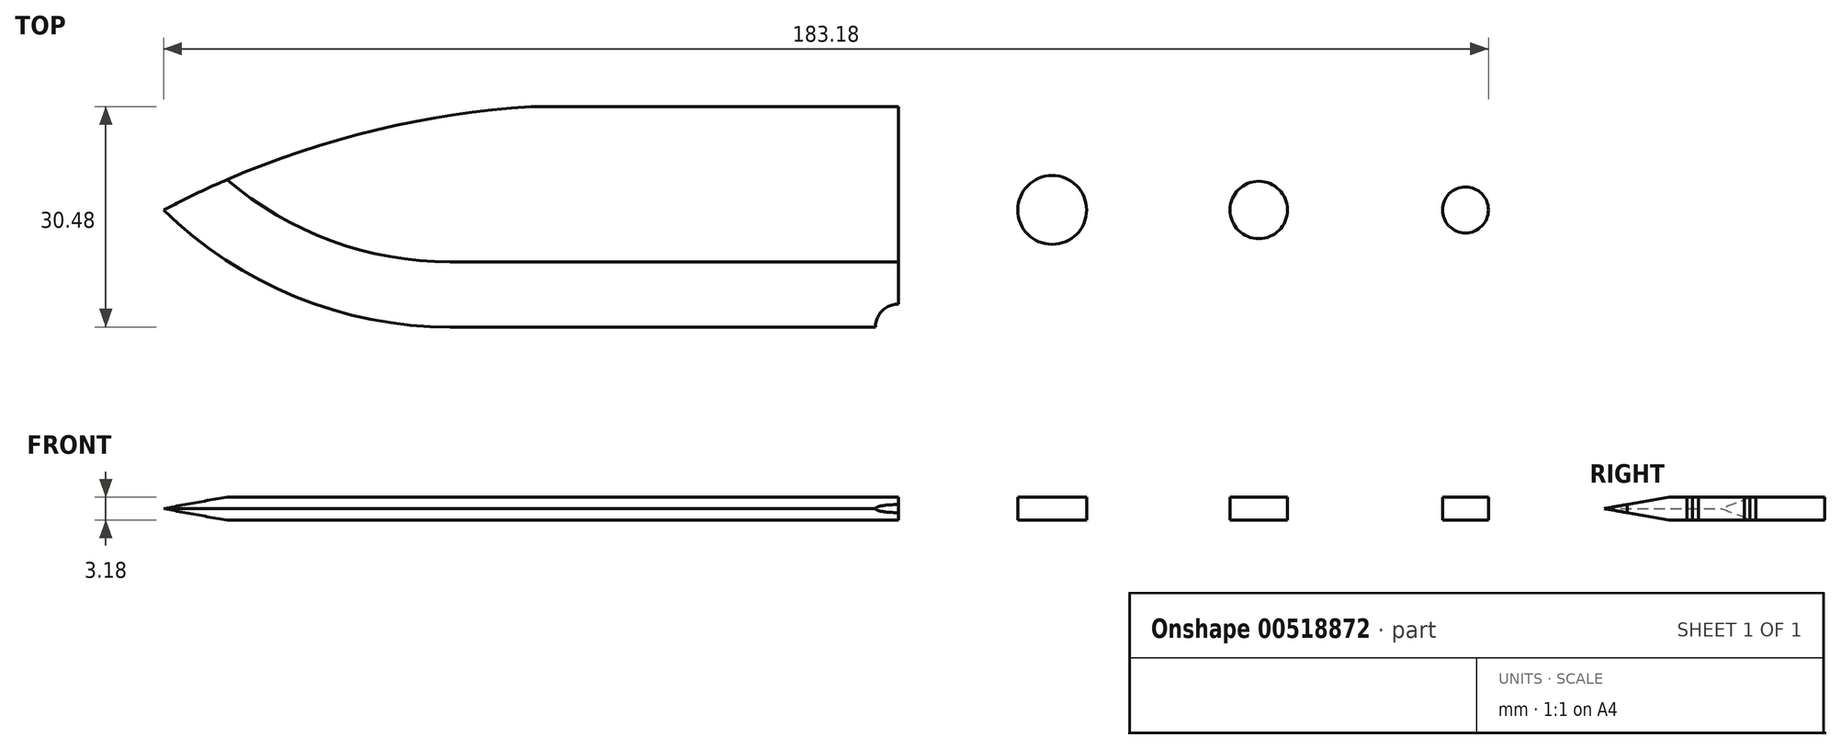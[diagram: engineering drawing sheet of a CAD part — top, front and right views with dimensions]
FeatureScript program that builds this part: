
annotation { "Feature Type Name" : "Feature", "Feature Type Description" : "" }
export const myFeature = defineFeature(function(context is Context, id is Id, definition is map)
    precondition{}
    {
        {
            var Q0;
            Q0=qCreatedBy(makeId("Top.planeOp"),FACE);
            var sketch = newSketch(context, id + "F0", { "sketchPlane" : qUnion([Q0])});
            skLineSegment(sketch, "E0", {"start": v(0, 0) * mm, "end": v(203.2, 0) * mm});
            skLineSegment(sketch, "E1", {"start": v(203.2, 0) * mm, "end": v(203.2, -38.1) * mm});
            skLineSegment(sketch, "E2", {"start": v(203.2, -38.1) * mm, "end": v(0, -38.1) * mm});
            skLineSegment(sketch, "E3", {"start": v(0, -38.1) * mm, "end": v(0, 0) * mm});
            skSolve(sketch);
        }
        {
            var Q0;
            Q0=qSketchRegion(id+"F0",true);
            extrude(context, id + "F1", {"entities" : qUnion([Q0]), "depth" : 3.17 * mm});
        }
        {
            var Q0;
            Q0=makeQuery(id+"F1.opExtrude","CAP_FACE",FACE,{"disambiguationData":[OSD([sQuery(id+"F0.wireOp",EDGE,"E0"),sQuery(id+"F0.wireOp",EDGE,"E1"),sQuery(id+"F0.wireOp",EDGE,"E2"),sQuery(id+"F0.wireOp",EDGE,"E3")])],"isStart":false});
            var sketch = newSketch(context, id + "F2", { "sketchPlane" : qUnion([Q0])});
            skLineSegment(sketch, "E4", {"start": v(101.6, 0) * mm, "end": v(101.6, -38.1) * mm});
            skLineSegment(sketch, "E5", {"start": v(0, 0) * mm, "end": v(0, -19.05) * mm});
            skLineSegment(sketch, "E6", {"start": v(0, -9.53) * mm, "end": v(0, -19.05) * mm});
            skLineSegment(sketch, "E7", {"start": v(0, 0) * mm, "end": v(101.6, 0) * mm});
            skLineSegment(sketch, "E8", {"start": v(39.6, -30.48) * mm, "end": v(101.6, -30.48) * mm});
            skArc(sketch, "E9", {"start": v(50.8, 0) * mm, "mid": v(24.65, -4.48) * mm, "end": v(0, -14.29) * mm});
            skCircle(sketch, "E10", {"center": v(101.6, -30.48) * mm, "radius": 3.18 * mm});
            skLineSegment(sketch, "E11", {"start": v(101.6, -30.48) * mm, "end": v(126.72, -30.48) * mm});
            skLineSegment(sketch, "E12", {"start": v(101.6, -33.65) * mm, "end": v(126.77, -33.65) * mm});
            skLineSegment(sketch, "E13", {"start": v(104.78, -30.48) * mm, "end": v(104.78, -33.65) * mm});
            skLineSegment(sketch, "E14", {"start": v(104.78, -33.65) * mm, "end": v(104.78, -38.1) * mm});
            skArc(sketch, "E15", {"start": v(134.38, -28.16) * mm, "mid": v(118.68, -26.05) * mm, "end": v(104.78, -33.66) * mm});
            skLineSegment(sketch, "E16", {"start": v(203.2, 0) * mm, "end": v(203.2, -19.05) * mm});
            skArc(sketch, "E17", {"start": v(193.68, -26.2) * mm, "mid": v(163.91, -23.67) * mm, "end": v(134.38, -28.16) * mm});
            skPoint(sketch, "E18", {"position": v(39.6, -30.48) * mm});
            skArc(sketch, "E19", {"start": v(0, -14.29) * mm, "mid": v(18.2, -26.28) * mm, "end": v(39.6, -30.48) * mm});
            skLineSegment(sketch, "E20", {"start": v(0, -14.29) * mm, "end": v(203.2, -14.29) * mm});
            skLineSegment(sketch, "E21", {"start": v(184.15, 0) * mm, "end": v(203.2, -14.29) * mm});
            skLineSegment(sketch, "E22", {"start": v(203.2, -14.29) * mm, "end": v(184.15, -38.1) * mm});
            skCircle(sketch, "E23", {"center": v(122.86, -14.29) * mm, "radius": 4.76 * mm});
            skCircle(sketch, "E24", {"center": v(180, -14.29) * mm, "radius": 3.18 * mm});
            skCircle(sketch, "E25", {"center": v(151.43, -14.29) * mm, "radius": 3.97 * mm});
            skSolve(sketch);
        }
        {
            var Q0;
            {var subQ0=sQuery(id+"F2.wireOp",EDGE,"E5");Q0=makeQuery(id+"F2.imprint","IMPRINT",FACE,{"disambiguationData":[TD([[makeQuery(id+"F2.imprint","IMPRINT",EDGE,{"derivedFrom":subQ0}),-1.0]])]});}
            var Q1;
            {var subQ0=sQuery(id+"F2.wireOp",EDGE,"hBmztbTj-tqe3-CgKz-6O3F-K7U5qk9btVsn");var subQ1=sQuery(id+"F2.wireOp",EDGE,"E8");var subQ2=makeQuery(id+"F2.imprint","INTERSECT",VERTEX,{"derivedFrom":[subQ1,subQ0]});Q1=makeQuery(id+"F2.imprint","IMPRINT",FACE,{"disambiguationData":[TD([[makeQuery(id+"F2.imprint","IMPRINT",EDGE,{"disambiguationData":[TD([[subQ2,-1.0]])],"derivedFrom":subQ1}),-1.0]])]});}
            var Q2;
            {var subQ5=sQuery(id+"F2.wireOp",EDGE,"E14");Q2=makeQuery(id+"F2.imprint","IMPRINT",FACE,{"disambiguationData":[TD([[makeQuery(id+"F2.imprint","IMPRINT",EDGE,{"derivedFrom":subQ5}),-1.0]])]});}
            var Q3;
            {var subQ3=sQuery(id+"F2.wireOp",EDGE,"E13");Q3=makeQuery(id+"F2.imprint","IMPRINT",FACE,{"disambiguationData":[TD([[makeQuery(id+"F2.imprint","IMPRINT",EDGE,{"derivedFrom":subQ3}),-1.0]])]});}
            var Q4;
            {var subQ0=sQuery(id+"F2.wireOp",EDGE,"E11");var subQ1=sQuery(id+"F2.wireOp",EDGE,"E4");var subQ2=makeQuery(id+"F2.imprint","INTERSECT",VERTEX,{"derivedFrom":[subQ1,sQuery(id+"F2.wireOp",EDGE,"E8"),subQ0]});Q4=makeQuery(id+"F2.imprint","IMPRINT",FACE,{"disambiguationData":[TD([[makeQuery(id+"F2.imprint","IMPRINT",EDGE,{"disambiguationData":[TD([[subQ2,-1.0]])],"derivedFrom":subQ1}),1.0]])]});}
            var Q5;
            {var subQ1=sQuery(id+"F2.wireOp",EDGE,"E4");var subQ3=sQuery(id+"F2.wireOp",EDGE,"E10");var subQ4=makeQuery(id+"F2.imprint","INTERSECT",VERTEX,{"derivedFrom":[subQ1,subQ3]});Q5=makeQuery(id+"F2.imprint","IMPRINT",FACE,{"disambiguationData":[TD([[makeQuery(id+"F2.imprint","IMPRINT",EDGE,{"disambiguationData":[TD([[subQ4,-1.0]])],"derivedFrom":subQ1}),1.0]])]});}
            var Q6;
            {var subQ1=sQuery(id+"F2.wireOp",EDGE,"E4");var subQ3=sQuery(id+"F2.wireOp",EDGE,"E10");var subQ4=makeQuery(id+"F2.imprint","INTERSECT",VERTEX,{"derivedFrom":[subQ1,subQ3]});Q6=makeQuery(id+"F2.imprint","IMPRINT",FACE,{"disambiguationData":[TD([[makeQuery(id+"F2.imprint","IMPRINT",EDGE,{"disambiguationData":[TD([[subQ4,-1.0]])],"derivedFrom":subQ3}),1.0]])]});}
            var Q7;
            {var subQ0=sQuery(id+"F2.wireOp",EDGE,"E8");var subQ3=sQuery(id+"F2.wireOp",EDGE,"E10");var subQ5=makeQuery(id+"F2.imprint","INTERSECT",VERTEX,{"derivedFrom":[subQ0,subQ3]});Q7=makeQuery(id+"F2.imprint","IMPRINT",FACE,{"disambiguationData":[TD([[makeQuery(id+"F2.imprint","IMPRINT",EDGE,{"disambiguationData":[TD([[subQ5,-1.0]])],"derivedFrom":subQ0}),-1.0]])]});}
            var Q8;
            {var subQ1=sQuery(id+"F2.wireOp",EDGE,"E14");Q8=makeQuery(id+"F2.imprint","IMPRINT",FACE,{"disambiguationData":[TD([[makeQuery(id+"F2.imprint","IMPRINT",EDGE,{"derivedFrom":subQ1}),1.0]])]});}
            var Q9;
            {var subQ0=sQuery(id+"F2.wireOp",EDGE,"locTSA2M-AsP4-2HM6-qX5g-so1iKQziUQEc");var subQ4=makeQuery(id+"F2.imprint","INTERSECT",VERTEX,{"derivedFrom":[subQ0,sQuery(id+"F2.wireOp",EDGE,"E17")]});Q9=makeQuery(id+"F2.imprint","IMPRINT",FACE,{"disambiguationData":[TD([[makeQuery(id+"F2.imprint","IMPRINT",EDGE,{"disambiguationData":[TD([[subQ4,-1.0]])],"derivedFrom":subQ0}),1.0]])]});}
            var Q10;
            {var subQ0=sQuery(id+"F2.wireOp",EDGE,"locTSA2M-AsP4-2HM6-qX5g-so1iKQziUQEc");var subQ3=sQuery(id+"F2.wireOp",EDGE,"E17");var subQ5=makeQuery(id+"F2.imprint","INTERSECT",VERTEX,{"derivedFrom":[subQ0,subQ3]});Q10=makeQuery(id+"F2.imprint","IMPRINT",FACE,{"disambiguationData":[TD([[makeQuery(id+"F2.imprint","IMPRINT",EDGE,{"disambiguationData":[TD([[subQ5,-1.0]])],"derivedFrom":subQ3}),1.0]])]});}
            var Q11;
            {var subQ1=sQuery(id+"F2.wireOp",EDGE,"pldBipSu-5jdq-XlzJ-CgNP-Urclp5KgjKv2");var subQ3=sQuery(id+"F2.wireOp",EDGE,"hBmztbTj-tqe3-CgKz-6O3F-K7U5qk9btVsn");var subQ4=makeQuery(id+"F2.imprint","INTERSECT",VERTEX,{"derivedFrom":[subQ1,subQ3]});Q11=makeQuery(id+"F2.imprint","IMPRINT",FACE,{"disambiguationData":[TD([[makeQuery(id+"F2.imprint","IMPRINT",EDGE,{"disambiguationData":[TD([[subQ4,1.0]])],"derivedFrom":subQ1}),1.0]])]});}
            var Q12;
            {var subQ3=sQuery(id+"F2.wireOp",EDGE,"E8");var subQ9=sQuery(id+"F2.wireOp",EDGE,"E19");var subQ10=makeQuery(id+"F2.imprint","INTERSECT",VERTEX,{"derivedFrom":[subQ3,subQ9]});Q12=makeQuery(id+"F2.imprint","IMPRINT",FACE,{"disambiguationData":[TD([[makeQuery(id+"F2.imprint","IMPRINT",EDGE,{"disambiguationData":[TD([[subQ10,-1.0]])],"derivedFrom":subQ3}),-1.0]])]});}
            var Q13;
            {var subQ0=sQuery(id+"F2.wireOp",EDGE,"E16");Q13=makeQuery(id+"F2.imprint","IMPRINT",FACE,{"disambiguationData":[TD([[makeQuery(id+"F2.imprint","IMPRINT",EDGE,{"derivedFrom":subQ0}),-1.0]])]});}
            var Q14;
            {var subQ5=sQuery(id+"F2.wireOp",EDGE,"E22");var subQ6=makeQuery(id+"F2.imprint","INTERSECT",VERTEX,{"derivedFrom":[sQuery(id+"F2.wireOp",EDGE,"E17"),subQ5]});Q14=makeQuery(id+"F2.imprint","IMPRINT",FACE,{"disambiguationData":[TD([[makeQuery(id+"F2.imprint","IMPRINT",EDGE,{"disambiguationData":[TD([[subQ6,-1.0]])],"derivedFrom":subQ5}),1.0]])]});}
            var Q15;
            {var subQ0=sQuery(id+"F2.wireOp",EDGE,"E13");Q15=makeQuery(id+"F2.imprint","IMPRINT",FACE,{"disambiguationData":[TD([[makeQuery(id+"F2.imprint","IMPRINT",EDGE,{"derivedFrom":subQ0}),1.0]])]});}
            var Q16;
            {var subQ0=sQuery(id+"F2.wireOp",EDGE,"E23");var subQ1=sQuery(id+"F2.wireOp",EDGE,"E20");var subQ2=makeQuery(id+"F2.imprint","INTERSECT",VERTEX,{"disambiguationData":[OD(0.0)],"derivedFrom":[subQ1,subQ0]});Q16=makeQuery(id+"F2.imprint","IMPRINT",FACE,{"disambiguationData":[TD([[makeQuery(id+"F2.imprint","IMPRINT",EDGE,{"disambiguationData":[TD([[subQ2,-1.0]])],"derivedFrom":subQ1}),1.0]])]});}
            var Q17;
            {var subQ0=sQuery(id+"F2.wireOp",EDGE,"E23");var subQ1=sQuery(id+"F2.wireOp",EDGE,"E20");var subQ2=makeQuery(id+"F2.imprint","INTERSECT",VERTEX,{"disambiguationData":[OD(0.0)],"derivedFrom":[subQ1,subQ0]});Q17=makeQuery(id+"F2.imprint","IMPRINT",FACE,{"disambiguationData":[TD([[makeQuery(id+"F2.imprint","IMPRINT",EDGE,{"disambiguationData":[TD([[subQ2,-1.0]])],"derivedFrom":subQ1}),-1.0]])]});}
            var Q18;
            {var subQ0=sQuery(id+"F2.wireOp",EDGE,"E24");var subQ1=sQuery(id+"F2.wireOp",EDGE,"E20");var subQ2=makeQuery(id+"F2.imprint","INTERSECT",VERTEX,{"disambiguationData":[OD(0.0)],"derivedFrom":[subQ1,subQ0]});Q18=makeQuery(id+"F2.imprint","IMPRINT",FACE,{"disambiguationData":[TD([[makeQuery(id+"F2.imprint","IMPRINT",EDGE,{"disambiguationData":[TD([[subQ2,-1.0]])],"derivedFrom":subQ1}),1.0]])]});}
            var Q19;
            {var subQ0=sQuery(id+"F2.wireOp",EDGE,"E24");var subQ1=sQuery(id+"F2.wireOp",EDGE,"E20");var subQ2=makeQuery(id+"F2.imprint","INTERSECT",VERTEX,{"disambiguationData":[OD(0.0)],"derivedFrom":[subQ1,subQ0]});Q19=makeQuery(id+"F2.imprint","IMPRINT",FACE,{"disambiguationData":[TD([[makeQuery(id+"F2.imprint","IMPRINT",EDGE,{"disambiguationData":[TD([[subQ2,-1.0]])],"derivedFrom":subQ1}),-1.0]])]});}
            var Q20;
            {var subQ0=sQuery(id+"F2.wireOp",EDGE,"E25");var subQ1=sQuery(id+"F2.wireOp",EDGE,"E20");var subQ2=makeQuery(id+"F2.imprint","INTERSECT",VERTEX,{"disambiguationData":[OD(0.0)],"derivedFrom":[subQ1,subQ0]});Q20=makeQuery(id+"F2.imprint","IMPRINT",FACE,{"disambiguationData":[TD([[makeQuery(id+"F2.imprint","IMPRINT",EDGE,{"disambiguationData":[TD([[subQ2,-1.0]])],"derivedFrom":subQ1}),1.0]])]});}
            var Q21;
            {var subQ0=sQuery(id+"F2.wireOp",EDGE,"E25");var subQ1=sQuery(id+"F2.wireOp",EDGE,"E20");var subQ2=makeQuery(id+"F2.imprint","INTERSECT",VERTEX,{"disambiguationData":[OD(0.0)],"derivedFrom":[subQ1,subQ0]});Q21=makeQuery(id+"F2.imprint","IMPRINT",FACE,{"disambiguationData":[TD([[makeQuery(id+"F2.imprint","IMPRINT",EDGE,{"disambiguationData":[TD([[subQ2,-1.0]])],"derivedFrom":subQ1}),-1.0]])]});}
            extrude(context, id + "F3", {"entities" : qUnion([Q0, Q1, Q2, Q3, Q4, Q5, Q6, Q7, Q8, Q9, Q10, Q11, Q12, Q13, Q14, Q15, Q16, Q17, Q18, Q19, Q20, Q21]), "operationType" : NewBodyOperationType.REMOVE, "oppositeDirection" : true, "depth" : 25.4 * mm});
        }
        {
            var Q0;
            {var subQ0=sQuery(id+"F2.wireOp",EDGE,"E19");Q0=makeQuery(id+"F2.imprint","IMPRINT",FACE,{"disambiguationData":[TD([[makeQuery(id+"F2.imprint","IMPRINT",EDGE,{"derivedFrom":subQ0}),1.0]])]});}
            cPlane(context, id + "F4", {"entities" : qUnion([Q0]), "cplaneType" : CPlaneType.OFFSET, "offset" : 1.59 * mm, "oppositeDirection" : true, "width" : 152.4 * mm, "height" : 152.4 * mm});
        }
        {
            var Q0;
            Q0=qCreatedBy(id+"F4.planeOp",FACE);
            var sketch = newSketch(context, id + "F5", { "sketchPlane" : qUnion([Q0])});
            skLineSegment(sketch, "E26", {"start": v(39.6, -30.48) * mm, "end": v(101.6, -30.48) * mm});
            skArc(sketch, "E27", {"start": v(0, -14.29) * mm, "mid": v(18.2, -26.28) * mm, "end": v(39.6, -30.48) * mm});
            skPoint(sketch, "E28", {"position": v(101.6, -30.48) * mm});
            skSolve(sketch);
        }
        {
            var Q0;
            Q0=qCreatedBy(makeId("Right.planeOp"),FACE);
            cPlane(context, id + "F6", {"entities" : qUnion([Q0]), "cplaneType" : CPlaneType.OFFSET, "offset" : 101.6 * mm, "width" : 152.4 * mm, "height" : 152.4 * mm});
        }
        {
            var Q0;
            Q0=qCreatedBy(id+"F6.planeOp",FACE);
            var sketch = newSketch(context, id + "F7", { "sketchPlane" : qUnion([Q0])});
            skLineSegment(sketch, "E29", {"start": v(-30.48, 0) * mm, "end": v(-30.48, 1.59) * mm});
            skLineSegment(sketch, "E30", {"start": v(-30.48, 3.19) * mm, "end": v(-30.48, 1.59) * mm});
            skLineSegment(sketch, "E31", {"start": v(-30.48, 1.59) * mm, "end": v(-3.22, 1.59) * mm});
            skLineSegment(sketch, "E32", {"start": v(-30.48, 1.59) * mm, "end": v(-4.12, 6.24) * mm});
            skLineSegment(sketch, "E33.MirrorCS", {"start": v(-30.48, 1.59) * mm, "end": v(-4.12, -3.06) * mm});
            skLineSegment(sketch, "E34", {"start": v(-4.12, -3.06) * mm, "end": v(-30.48, -3.06) * mm});
            skLineSegment(sketch, "E35", {"start": v(-30.48, -3.06) * mm, "end": v(-30.48, 1.59) * mm});
            skLineSegment(sketch, "E36", {"start": v(-4.12, 6.24) * mm, "end": v(-30.48, 6.24) * mm});
            skLineSegment(sketch, "E37", {"start": v(-30.48, 6.24) * mm, "end": v(-30.48, 1.59) * mm});
            skSolve(sketch);
        }
        {
            var Q0;
            Q0=qSketchRegion(id+"F7",true);
            var Q1;
            Q1=qConstructionFilter(qBodyType(qCreatedBy(id+"F5",EDGE),BodyType.WIRE),ConstructionObject.NO);
            sweep(context, id + "F8", {"operationType" : NewBodyOperationType.REMOVE, "profiles" : qUnion([Q0]), "path" : qUnion([Q1])});
        }
    });
